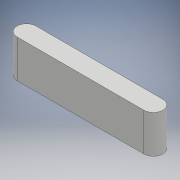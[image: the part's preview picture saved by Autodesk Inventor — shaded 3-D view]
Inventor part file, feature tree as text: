
AUTODESK INVENTOR PART (.ipt)
format: ipt  version: 2018 (Build 220112000, 112)  size: 94,208 bytes
history: native  units: mm
features: extrude x1, sketch x1
ambient origin geometry x8: Origin, YZ Plane, XZ Plane, XY Plane, X Axis, Y Axis, Z Axis, Center Point
bodies: Solid1 (feature_tree)
feature tree (2):
  extrude  "Extrusion1"  Depth=10.0mm
  sketch  "Sketch1"  dims[d0=1.3mm d1=10.0mm d2=8.7mm d3=2.6mm d4=0.0mm]
